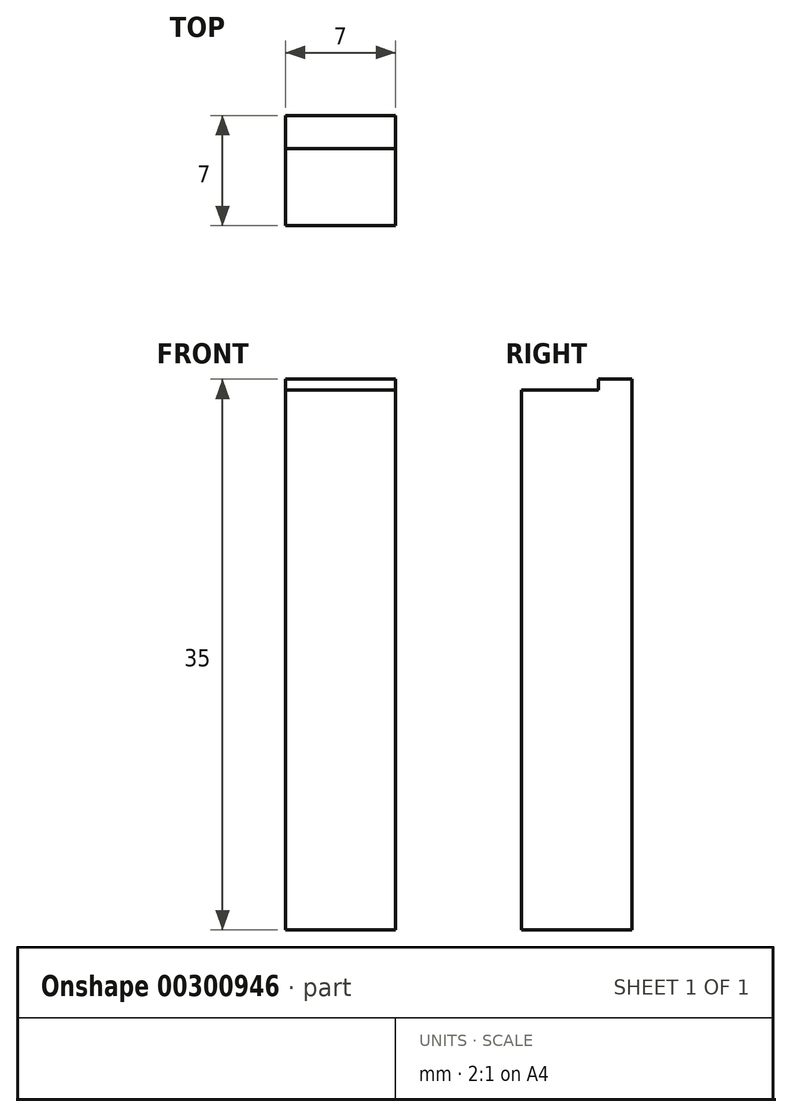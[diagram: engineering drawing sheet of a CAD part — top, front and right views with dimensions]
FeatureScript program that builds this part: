
annotation { "Feature Type Name" : "Feature", "Feature Type Description" : "" }
export const myFeature = defineFeature(function(context is Context, id is Id, definition is map)
    precondition{}
    {
        {
            var Q0;
            Q0=qCreatedBy(makeId("Front.planeOp"),FACE);
            var sketch = newSketch(context, id + "F0", { "sketchPlane" : qUnion([Q0])});
            skLineSegment(sketch, "E0.bottom", {"start": v(0, 0) * mm, "end": v(100, 0) * mm});
            skLineSegment(sketch, "E0.top", {"start": v(0, 500) * mm, "end": v(100, 500) * mm});
            skLineSegment(sketch, "E0.left", {"start": v(0, 0) * mm, "end": v(0, 500) * mm});
            skLineSegment(sketch, "E0.right", {"start": v(100, 0) * mm, "end": v(100, 500) * mm});
            skSolve(sketch);
        }
        {
            var Q0;
            Q0=qSketchRegion(id+"F0",true);
            extrude(context, id + "F1", {"entities" : qUnion([Q0]), "depth" : 100 * mm});
        }
        {
            var Q0;
            Q0=makeQuery(id+"F1.opExtrude","SWEPT_FACE",FACE,{"disambiguationData":[OSD([sQuery(id+"F0.wireOp",EDGE,"E0.top")])]});
            var sketch = newSketch(context, id + "F2", { "sketchPlane" : qUnion([Q0])});
            skLineSegment(sketch, "E1.bottom", {"start": v(0, -100) * mm, "end": v(100, -100) * mm});
            skLineSegment(sketch, "E1.top", {"start": v(0, -30) * mm, "end": v(100, -30) * mm});
            skLineSegment(sketch, "E1.left", {"start": v(0, -100) * mm, "end": v(0, -30) * mm});
            skLineSegment(sketch, "E1.right", {"start": v(100, -100) * mm, "end": v(100, -30) * mm});
            skSolve(sketch);
        }
        {
            var Q0;
            Q0=makeQuery(id+"F2.imprint","IMPRINT",FACE,{"disambiguationData":[TD([[makeQuery(id+"F2.imprint","IMPRINT",EDGE,{"derivedFrom":sQuery(id+"F2.wireOp",EDGE,"E1.bottom")}),1.0]])]});
            extrude(context, id + "F3", {"entities" : qUnion([Q0]), "operationType" : NewBodyOperationType.REMOVE, "oppositeDirection" : true, "depth" : 10 * mm});
        }
        {
            var Q0;
            Q0=makeQuery(id+"F1.opExtrude","SWEPT_BODY",BODY,{"disambiguationData":[OSD([sQuery(id+"F0.wireOp",EDGE,"E0.bottom"),sQuery(id+"F0.wireOp",EDGE,"E0.top"),sQuery(id+"F0.wireOp",EDGE,"E0.left"),sQuery(id+"F0.wireOp",EDGE,"E0.right")])]});
            var Q1;
            Q1=qCreatedBy(makeId("Origin.pointOp"),VERTEX);
            transform(context, id + "F4", {"entities" : qUnion([Q0]), "transformType" : TransformType.SCALE_UNIFORMLY, "scale" : 0.07, "scalePoint" : qUnion([Q1]), "makeCopy" : false});
        }
    });
